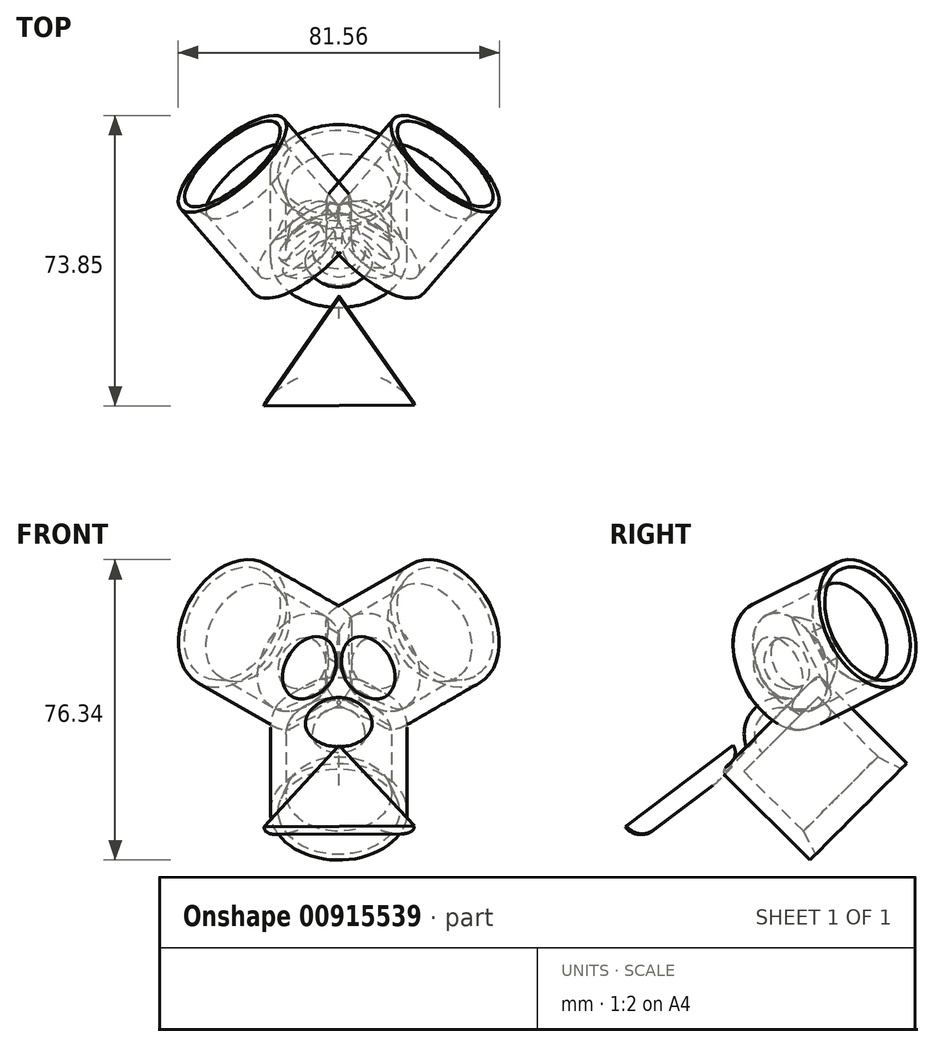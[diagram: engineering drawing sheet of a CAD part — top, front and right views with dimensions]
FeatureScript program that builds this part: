
annotation { "Feature Type Name" : "Feature", "Feature Type Description" : "" }
export const myFeature = defineFeature(function(context is Context, id is Id, definition is map)
    precondition{}
    {
        {
            var Q0;
            Q0=qCreatedBy(makeId("Front.planeOp"),FACE);
            var sketch = newSketch(context, id + "F0", { "sketchPlane" : qUnion([Q0])});
            skLineSegment(sketch, "E0", {"start": v(-65.6, 0) * mm, "end": v(95.42, 0) * mm, "construction": true});
            skLineSegment(sketch, "E1.left", {"start": v(-13.4, 12.88) * mm, "end": v(-13.4, -12.88) * mm, "construction": true});
            skLineSegment(sketch, "E1.right", {"start": v(13.39, 12.88) * mm, "end": v(13.4, -8.56) * mm});
            skPoint(sketch, "E1.middle", {"position": v(0, 0) * mm});
            skLineSegment(sketch, "E2.left", {"start": v(-15.41, 14.9) * mm, "end": v(-15.41, -14.9) * mm, "construction": true});
            skLineSegment(sketch, "E3", {"start": v(15.41, 14.9) * mm, "end": v(0, 41.6) * mm, "construction": true});
            skLineSegment(sketch, "E4", {"start": v(-15.41, 14.9) * mm, "end": v(0, 41.6) * mm, "construction": true});
            skPoint(sketch, "E5", {"position": v(0, 23.8) * mm});
            skPoint(sketch, "E6.endSnap0", {"position": v(7.7, 14.9) * mm});
            skPoint(sketch, "E7", {"position": v(0, 12.88) * mm});
            skPoint(sketch, "E8", {"position": v(0, 14.9) * mm});
            skLineSegment(sketch, "E9", {"start": v(9.37, 12.88) * mm, "end": v(13.39, 12.88) * mm});
            skLineSegment(sketch, "E10", {"start": v(-13.4, 12.88) * mm, "end": v(9.37, 12.88) * mm, "construction": true});
            skLineSegment(sketch, "E11", {"start": v(-15.41, 14.9) * mm, "end": v(9.37, 14.9) * mm, "construction": true});
            skLineSegment(sketch, "E12", {"start": v(0, 0) * mm, "end": v(0, 25.56) * mm, "construction": true});
            skArc(sketch, "E13", {"start": v(6.73, 12.88) * mm, "mid": v(4.76, 17.64) * mm, "end": v(0, 19.61) * mm});
            skArc(sketch, "E14", {"start": v(8.47, 16.88) * mm, "mid": v(5.01, 20.8) * mm, "end": v(0, 22.25) * mm});
            skLineSegment(sketch, "E15", {"start": v(9.37, 12.88) * mm, "end": v(6.73, 12.88) * mm});
            skLineSegment(sketch, "E16", {"start": v(0, 22.25) * mm, "end": v(0, 19.61) * mm});
            skLineSegment(sketch, "E17", {"start": v(13.39, 7.3) * mm, "end": v(17.4, 7.3) * mm, "construction": true});
            skLineSegment(sketch, "E18", {"start": v(17.4, 16.88) * mm, "end": v(17.4, -14.9) * mm});
            skLineSegment(sketch, "E19", {"start": v(15.4, -14.9) * mm, "end": v(17.4, -14.9) * mm});
            skLineSegment(sketch, "E20", {"start": v(17.4, 16.88) * mm, "end": v(8.47, 16.88) * mm});
            skPoint(sketch, "E21.orphan", {"position": v(17.4, 14.9) * mm});
            skLineSegment(sketch, "E22", {"start": v(15.4, -14.9) * mm, "end": v(13.39, -8.56) * mm});
            skPoint(sketch, "E23.end.orphan", {"position": v(13.4, -14.9) * mm});
            skLineSegment(sketch, "E24", {"start": v(6.73, 12.88) * mm, "end": v(0, 12.88) * mm});
            skLineSegment(sketch, "E25", {"start": v(0, -10.14) * mm, "end": v(13.4, -10.14) * mm});
            skLineSegment(sketch, "E26", {"start": v(13.39, -10.14) * mm, "end": v(13.39, -8.56) * mm});
            skLineSegment(sketch, "E27", {"start": v(0, -10.14) * mm, "end": v(0, 12.88) * mm});
            skSolve(sketch);
        }
        {
            var Q0;
            Q0=makeQuery(id+"F0.imprint","IMPRINT",FACE,{"disambiguationData":[TD([[makeQuery(id+"F0.imprint","IMPRINT",EDGE,{"derivedFrom":sQuery(id+"F0.wireOp",EDGE,"E1.right")}),1.0]])]});
            var Q1;
            Q1=sQuery(id+"F0.wireOp",EDGE,"E12");
            revolve(context, id + "F1", {"surfaceOperationType" : NewSurfaceOperationType.NEW, "entities" : qUnion([Q0]), "axis" : qUnion([Q1]), "revolveType" : RevolveType.FULL});
        }
        {
            var Q0;
            Q0=makeQuery(id+"F1.opRevolve","SWEPT_EDGE",EDGE,{"disambiguationData":[OSD([sQuery(id+"F0.wireOp",EDGE,"E18"),sQuery(id+"F0.wireOp",EDGE,"E20")])]});
            fillet(context, id + "F2", {"entities" : qUnion([Q0]), "radius" : 1.5 * mm, "tangentPropagation" : true, "allowEdgeOverflow" : false});
        }
        {
            var Q0;
            Q0=qCreatedBy(makeId("Right.planeOp"),FACE);
            var sketch = newSketch(context, id + "F3", { "sketchPlane" : qUnion([Q0])});
            skLineSegment(sketch, "E28", {"start": v(-35.53, 26) * mm, "end": v(8.3, 26) * mm, "construction": true});
            skLineSegment(sketch, "E29", {"start": v(8.28, 30.68) * mm, "end": v(-35.5, 30.68) * mm, "construction": true});
            skSolve(sketch);
        }
        {
            var Q0;
            Q0=makeQuery(id+"F1.opRevolve","SWEPT_BODY",BODY,{"disambiguationData":[OSD([sQuery(id+"F0.wireOp",EDGE,"E1.right"),sQuery(id+"F0.wireOp",EDGE,"E2.right"),sQuery(id+"F0.wireOp",EDGE,"E23"),sQuery(id+"F0.wireOp",EDGE,"bP7MgH2K-PIgu-sQjO-5KmN-4AKa93nuKyW7"),sQuery(id+"F0.wireOp",EDGE,"E6"),sQuery(id+"F0.wireOp",EDGE,"L42gxlVk-bAQj-lGxW-YQ5i-IcCWysg2b6hQ"),sQuery(id+"F0.wireOp",EDGE,"E9")])]});
            var Q1;
            Q1=sQuery(id+"F3.wireOp",EDGE,"E28");
            circularPattern(context, id + "F4", {"entities" : qUnion([Q0]), "axis" : qUnion([Q1]), "angle" : 360 * degree, "instanceCount" : 3, "equalSpace" : true});
        }
        {
            var Q0;
            Q0=makeQuery(id+"F0.imprint","IMPRINT",FACE,{"disambiguationData":[TD([[makeQuery(id+"F0.imprint","IMPRINT",EDGE,{"derivedFrom":sQuery(id+"F0.wireOp",EDGE,"E1.right")}),-1.0]])]});
            var Q1;
            Q1=sQuery(id+"F0.wireOp",EDGE,"E27");
            revolve(context, id + "F5", {"operationType" : NewBodyOperationType.REMOVE, "surfaceOperationType" : NewSurfaceOperationType.NEW, "entities" : qUnion([Q0]), "axis" : qUnion([Q1]), "revolveType" : RevolveType.FULL});
        }
        {
            var Q0;
            Q0=makeQuery(id+"F1.opRevolve","SWEPT_BODY",BODY,{"disambiguationData":[OSD([sQuery(id+"F0.wireOp",EDGE,"E1.right"),sQuery(id+"F0.wireOp",EDGE,"E2.right"),sQuery(id+"F0.wireOp",EDGE,"u6sGE5v3-QqYS-glfV-MdEO-LVSjNsrG9YqO"),sQuery(id+"F0.wireOp",EDGE,"e8LDt0c8-95OP-7SPG-cx0F-moiXSnHBQ2JR"),sQuery(id+"F0.wireOp",EDGE,"Aw2z7rFZ-ruUb-1NY8-J7V9-fNkVEHLTtg4K"),sQuery(id+"F0.wireOp",EDGE,"E23"),sQuery(id+"F0.wireOp",EDGE,"bP7MgH2K-PIgu-sQjO-5KmN-4AKa93nuKyW7")])]});
            var Q1;
            Q1=sQuery(id+"F0.wireOp",EDGE,"E11");
            transform(context, id + "F6", {"entities" : qUnion([Q0]), "transformType" : TransformType.ROTATION, "transformAxis" : qUnion([Q1]), "angle" : 45 * degree, "makeCopy" : false});
        }
        {
            var Q0;
            Q0=makeQuery(id+"F4.opPattern","COPY",BODY,{"derivedFrom":makeQuery(id+"F1.opRevolve","SWEPT_BODY",BODY,{"disambiguationData":[OSD([sQuery(id+"F0.wireOp",EDGE,"E1.right"),sQuery(id+"F0.wireOp",EDGE,"E2.right"),sQuery(id+"F0.wireOp",EDGE,"u6sGE5v3-QqYS-glfV-MdEO-LVSjNsrG9YqO"),sQuery(id+"F0.wireOp",EDGE,"e8LDt0c8-95OP-7SPG-cx0F-moiXSnHBQ2JR"),sQuery(id+"F0.wireOp",EDGE,"Aw2z7rFZ-ruUb-1NY8-J7V9-fNkVEHLTtg4K"),sQuery(id+"F0.wireOp",EDGE,"E23"),sQuery(id+"F0.wireOp",EDGE,"bP7MgH2K-PIgu-sQjO-5KmN-4AKa93nuKyW7")])]}),"instanceName":"1"});
            var Q1;
            Q1=sQuery(id+"F0.wireOp",EDGE,"E4");
            transform(context, id + "F7", {"entities" : qUnion([Q0]), "transformType" : TransformType.ROTATION, "transformAxis" : qUnion([Q1]), "angle" : 45 * degree, "oppositeDirection" : true, "makeCopy" : false});
        }
        {
            var Q0;
            Q0=makeQuery(id+"F4.opPattern","COPY",BODY,{"derivedFrom":makeQuery(id+"F1.opRevolve","SWEPT_BODY",BODY,{"disambiguationData":[OSD([sQuery(id+"F0.wireOp",EDGE,"E1.right"),sQuery(id+"F0.wireOp",EDGE,"E2.right"),sQuery(id+"F0.wireOp",EDGE,"u6sGE5v3-QqYS-glfV-MdEO-LVSjNsrG9YqO"),sQuery(id+"F0.wireOp",EDGE,"e8LDt0c8-95OP-7SPG-cx0F-moiXSnHBQ2JR"),sQuery(id+"F0.wireOp",EDGE,"Aw2z7rFZ-ruUb-1NY8-J7V9-fNkVEHLTtg4K"),sQuery(id+"F0.wireOp",EDGE,"E23"),sQuery(id+"F0.wireOp",EDGE,"bP7MgH2K-PIgu-sQjO-5KmN-4AKa93nuKyW7")])]}),"instanceName":"2"});
            var Q1;
            Q1=sQuery(id+"F0.wireOp",EDGE,"E3");
            transform(context, id + "F8", {"entities" : qUnion([Q0]), "transformType" : TransformType.ROTATION, "transformAxis" : qUnion([Q1]), "angle" : 45 * degree, "makeCopy" : false});
        }
        {
            var Q0;
            Q0=makeQuery(id+"F1.opRevolve","SWEPT_FACE",FACE,{"disambiguationData":[OSD([sQuery(id+"F0.wireOp",EDGE,"E9"),sQuery(id+"F0.wireOp",EDGE,"E15")])]});
            extrude(context, id + "F9", {"entities" : qUnion([Q0]), "operationType" : NewBodyOperationType.REMOVE, "depth" : 27.8 * mm, "offsetDistance" : 25 * mm});
        }
        {
            var Q0;
            Q0=makeQuery(id+"F4.opPattern","COPY",FACE,{"derivedFrom":makeQuery(id+"F1.opRevolve","SWEPT_FACE",FACE,{"disambiguationData":[OSD([sQuery(id+"F0.wireOp",EDGE,"E9"),sQuery(id+"F0.wireOp",EDGE,"E15")])]}),"instanceName":"2"});
            extrude(context, id + "F10", {"entities" : qUnion([Q0]), "operationType" : NewBodyOperationType.REMOVE, "depth" : 27.8 * mm, "offsetDistance" : 25 * mm});
        }
        {
            var Q0;
            Q0=makeQuery(id+"F4.opPattern","COPY",FACE,{"derivedFrom":makeQuery(id+"F1.opRevolve","SWEPT_FACE",FACE,{"disambiguationData":[OSD([sQuery(id+"F0.wireOp",EDGE,"E9"),sQuery(id+"F0.wireOp",EDGE,"E15")])]}),"instanceName":"1"});
            extrude(context, id + "F11", {"entities" : qUnion([Q0]), "operationType" : NewBodyOperationType.REMOVE, "depth" : 27.8 * mm, "offsetDistance" : 25 * mm});
        }
        {
            var Q0;
            {var subQ0=sQuery(id+"F0.wireOp",EDGE,"E18");Q0=makeQuery(id+"F10.boolean.opBoolean","SPLIT",EDGE,{"disambiguationData":[OD(0.0)],"derivedFrom":makeQuery(id+"F4.opPattern","COPY",EDGE,{"derivedFrom":makeQuery(id+"F2.opFillet","BLEND_EDGE",EDGE,{"blendedFrom":[makeQuery(id+"F1.opRevolve","SWEPT_EDGE",EDGE,{"disambiguationData":[OSD([subQ0,sQuery(id+"F0.wireOp",EDGE,"E20")])]}),makeQuery(id+"F1.opRevolve","SWEPT_FACE",FACE,{"disambiguationData":[OSD([subQ0])]})],"blendedInto":[makeQuery(id+"F1.opRevolve","SWEPT_FACE",FACE,{"disambiguationData":[OSD([subQ0])]})]}),"instanceName":"1"})});}
            cPoint(context, id + "F12", {"entities" : qUnion([Q0]), "parameter" : 0.5});
        }
        {
            var Q0;
            {var subQ0=sQuery(id+"F0.wireOp",EDGE,"E18");Q0=makeQuery(id+"F11.boolean.opBoolean","SPLIT",EDGE,{"disambiguationData":[OD(0.0)],"derivedFrom":makeQuery(id+"F4.opPattern","COPY",EDGE,{"derivedFrom":makeQuery(id+"F2.opFillet","BLEND_EDGE",EDGE,{"blendedFrom":[makeQuery(id+"F1.opRevolve","SWEPT_EDGE",EDGE,{"disambiguationData":[OSD([subQ0,sQuery(id+"F0.wireOp",EDGE,"E20")])]}),makeQuery(id+"F1.opRevolve","SWEPT_FACE",FACE,{"disambiguationData":[OSD([subQ0])]})],"blendedInto":[makeQuery(id+"F1.opRevolve","SWEPT_FACE",FACE,{"disambiguationData":[OSD([subQ0])]})]}),"instanceName":"2"})});}
            cPoint(context, id + "F13", {"entities" : qUnion([Q0]), "parameter" : 0.5});
        }
        {
            var Q0;
            {var subQ0=sQuery(id+"F0.wireOp",EDGE,"E18");Q0=makeQuery(id+"F11.boolean.opBoolean","SPLIT",EDGE,{"disambiguationData":[OD(1.0)],"derivedFrom":makeQuery(id+"F2.opFillet","BLEND_EDGE",EDGE,{"blendedFrom":[makeQuery(id+"F1.opRevolve","SWEPT_EDGE",EDGE,{"disambiguationData":[OSD([subQ0,sQuery(id+"F0.wireOp",EDGE,"E20")])]}),makeQuery(id+"F1.opRevolve","SWEPT_FACE",FACE,{"disambiguationData":[OSD([subQ0])]})],"blendedInto":[makeQuery(id+"F1.opRevolve","SWEPT_FACE",FACE,{"disambiguationData":[OSD([subQ0])]})]})});}
            cPoint(context, id + "F14", {"entities" : qUnion([Q0]), "parameter" : 0.5});
        }
        {
            var Q0;
            Q0=qCreatedBy(id+"F12",VERTEX);
            var Q1;
            Q1=qCreatedBy(id+"F13",VERTEX);
            var Q2;
            Q2=qCreatedBy(id+"F14",VERTEX);
            cPlane(context, id + "F15", {"entities" : qUnion([Q0, Q1, Q2]), "cplaneType" : CPlaneType.THREE_POINT, "offset" : 25 * mm, "width" : 150 * mm, "height" : 150 * mm});
        }
        {
            var Q0;
            Q0=qCreatedBy(id+"F15.planeOp",FACE);
            var sketch = newSketch(context, id + "F16", { "sketchPlane" : qUnion([Q0])});
            skLineSegment(sketch, "E30", {"start": v(-18.98, 36.5) * mm, "end": v(19.19, 36.12) * mm});
            skLineSegment(sketch, "E31", {"start": v(0, 2.15) * mm, "end": v(19.19, 36.12) * mm});
            skLineSegment(sketch, "E32", {"start": v(-18.98, 36.5) * mm, "end": v(0, 2.15) * mm});
            skSolve(sketch);
        }
        {
            var Q0;
            Q0=makeQuery(id+"F16.imprint","IMPRINT",FACE,{"disambiguationData":[TD([[makeQuery(id+"F16.imprint","IMPRINT",EDGE,{"derivedFrom":sQuery(id+"F16.wireOp",EDGE,"E30")}),-1.0]])]});
            extrude(context, id + "F17", {"entities" : qUnion([Q0]), "oppositeDirection" : true, "depth" : 5 * mm, "offsetDistance" : 25 * mm});
        }
        {
            var Q0;
            Q0=makeQuery(id+"F17.opExtrude","CAP_EDGE",EDGE,{"disambiguationData":[OSD([sQuery(id+"F16.wireOp",EDGE,"E31")])],"isStart":true});
            var Q1;
            Q1=makeQuery(id+"F17.opExtrude","CAP_EDGE",EDGE,{"disambiguationData":[OSD([sQuery(id+"F16.wireOp",EDGE,"E30")])],"isStart":true});
            var Q2;
            Q2=makeQuery(id+"F17.opExtrude","CAP_EDGE",EDGE,{"disambiguationData":[OSD([sQuery(id+"F16.wireOp",EDGE,"E32")])],"isStart":true});
            fillet(context, id + "F18", {"entities" : qUnion([Q0, Q1, Q2]), "radius" : 5 * mm, "tangentPropagation" : true, "allowEdgeOverflow" : false});
        }
    });
